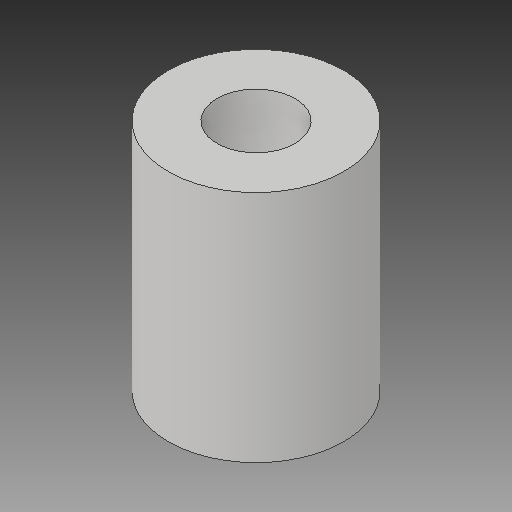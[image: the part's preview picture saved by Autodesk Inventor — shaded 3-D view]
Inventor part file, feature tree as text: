
AUTODESK INVENTOR PART (.ipt)
format: ipt  version: 2019 (Build 230136000, 136)  size: 94,208 bytes
history: native  units: in
note: dims shown in document units (in); Inventor stores cm internally (conversion verified against a paired STEP export)
features: extrude x1, sketch x1
ambient origin geometry x8: Origin, YZ Plane, XZ Plane, XY Plane, X Axis, Y Axis, Z Axis, Center Point
bodies: Solid1 (feature_tree)
feature tree (2):
  extrude  "Extrusion1"  Depth=0.9449in
  sketch  "Sketch1"  dims[d0=0.7087in d1=0.315in d2=0.9449in d3=0.0in]
